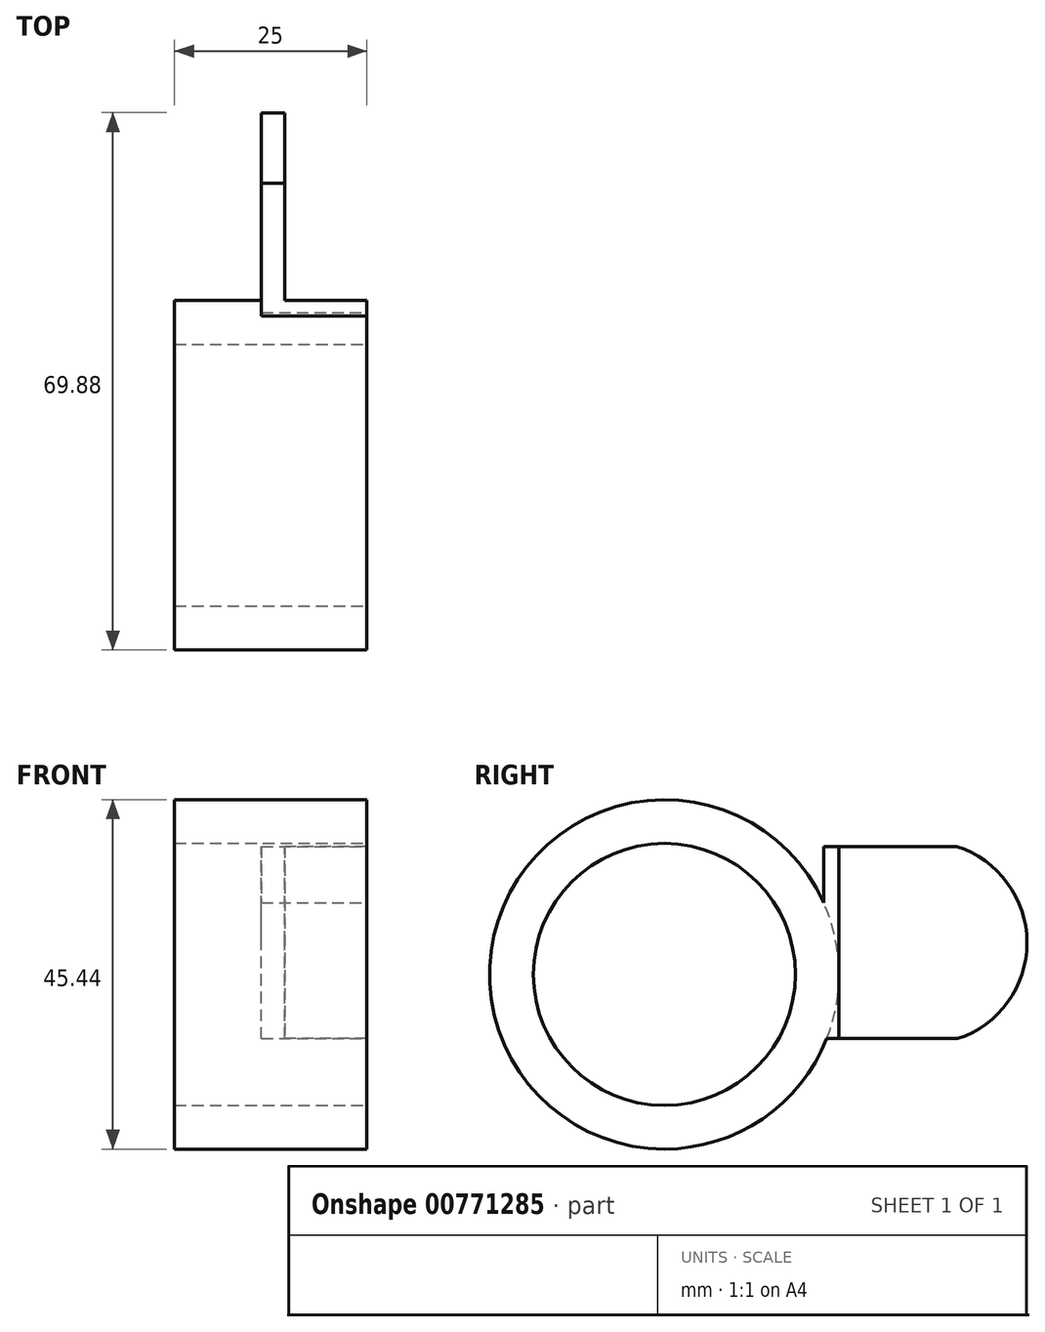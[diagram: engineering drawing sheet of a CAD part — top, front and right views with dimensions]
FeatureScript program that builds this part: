
annotation { "Feature Type Name" : "Feature", "Feature Type Description" : "" }
export const myFeature = defineFeature(function(context is Context, id is Id, definition is map)
    precondition{}
    {
        {
            var Q0;
            Q0=qCreatedBy(makeId("Top.planeOp"),FACE);
            var sketch = newSketch(context, id + "F0", { "sketchPlane" : qUnion([Q0])});
            skLineSegment(sketch, "E0", {"start": v(-10.64, 0) * mm, "end": v(-10.64, 24.44) * mm});
            skLineSegment(sketch, "E1", {"start": v(-10.64, 24.44) * mm, "end": v(-13.69, 24.44) * mm});
            skLineSegment(sketch, "E2", {"start": v(-13.69, 24.44) * mm, "end": v(-13.69, 0) * mm});
            skLineSegment(sketch, "E3", {"start": v(-13.69, 0) * mm, "end": v(-13.69, -2) * mm});
            skLineSegment(sketch, "E4", {"start": v(-13.69, -2) * mm, "end": v(0, -2) * mm});
            skLineSegment(sketch, "E5", {"start": v(0, -2) * mm, "end": v(0, 0) * mm});
            skLineSegment(sketch, "E6", {"start": v(0, 0) * mm, "end": v(-10.64, 0) * mm});
            skSolve(sketch);
        }
        {
            var Q0;
            Q0=makeQuery(id+"F0.imprint","IMPRINT",FACE,{"disambiguationData":[TD([[makeQuery(id+"F0.imprint","IMPRINT",EDGE,{"derivedFrom":sQuery(id+"F0.wireOp",EDGE,"E0")}),1.0]])]});
            extrude(context, id + "F1", {"entities" : qUnion([Q0]), "depth" : 25 * mm, "offsetDistance" : 25 * mm});
        }
        {
            var Q0;
            Q0=makeQuery(id+"F1.opExtrude","SWEPT_FACE",FACE,{"disambiguationData":[OSD([sQuery(id+"F0.wireOp",EDGE,"E0")])]});
            var sketch = newSketch(context, id + "F2", { "sketchPlane" : qUnion([Q0])});
            skArc(sketch, "E7", {"start": v(15.42, 0) * mm, "mid": v(24.44, 12.55) * mm, "end": v(15.28, 25) * mm});
            skLineSegment(sketch, "E8", {"start": v(15.28, 25) * mm, "end": v(24.44, 25) * mm});
            skLineSegment(sketch, "E9", {"start": v(24.44, 25) * mm, "end": v(24.44, 0) * mm});
            skLineSegment(sketch, "E10", {"start": v(24.44, 0) * mm, "end": v(15.42, 0) * mm});
            skSolve(sketch);
        }
        {
            var Q0;
            {var subQ0=sQuery(id+"F2.wireOp",EDGE,"E10");Q0=makeQuery(id+"F2.imprint","IMPRINT",FACE,{"disambiguationData":[TD([[makeQuery(id+"F2.imprint","IMPRINT",EDGE,{"derivedFrom":subQ0}),1.0]])]});}
            var Q1;
            {var subQ0=sQuery(id+"F2.wireOp",EDGE,"E8");Q1=makeQuery(id+"F2.imprint","IMPRINT",FACE,{"disambiguationData":[TD([[makeQuery(id+"F2.imprint","IMPRINT",EDGE,{"derivedFrom":subQ0}),-1.0]])]});}
            extrude(context, id + "F3", {"entities" : qUnion([Q0, Q1]), "operationType" : NewBodyOperationType.REMOVE, "oppositeDirection" : true, "depth" : 25 * mm, "offsetDistance" : 25 * mm});
        }
        {
            var Q0;
            Q0=qCreatedBy(makeId("Right.planeOp"),FACE);
            var sketch = newSketch(context, id + "F4", { "sketchPlane" : qUnion([Q0])});
            skCircle(sketch, "E11", {"center": v(-22.72, 8.36) * mm, "radius": 22.72 * mm});
            skCircle(sketch, "E12", {"center": v(-22.72, 8.36) * mm, "radius": 17.04 * mm});
            skSolve(sketch);
        }
        {
            var Q0;
            Q0=makeQuery(id+"F4.imprint","IMPRINT",FACE,{"disambiguationData":[TD([[makeQuery(id+"F4.imprint","IMPRINT",EDGE,{"derivedFrom":sQuery(id+"F4.wireOp",EDGE,"E11")}),1.0]])]});
            extrude(context, id + "F5", {"entities" : qUnion([Q0]), "operationType" : NewBodyOperationType.ADD, "oppositeDirection" : true, "depth" : 25 * mm, "offsetDistance" : 25 * mm});
        }
    });
